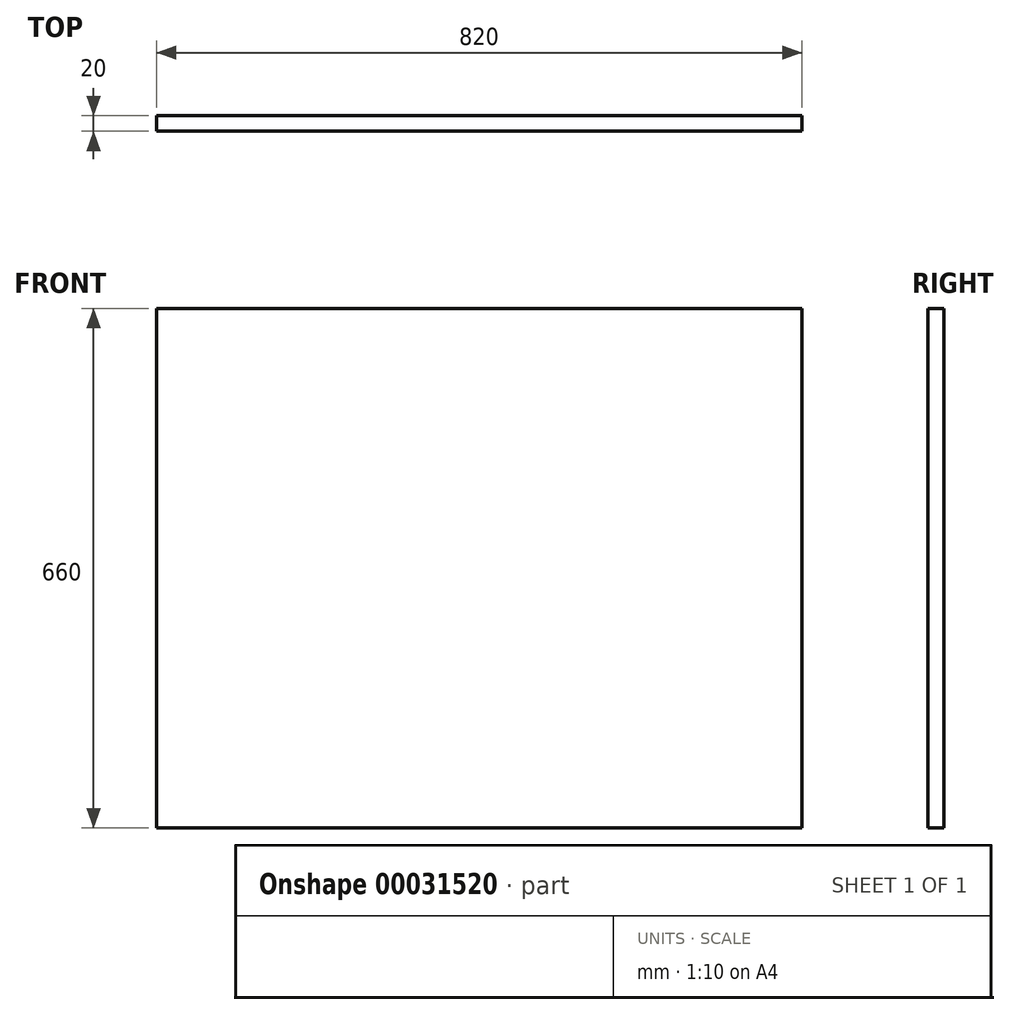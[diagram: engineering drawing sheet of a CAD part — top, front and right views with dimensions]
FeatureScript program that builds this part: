
annotation { "Feature Type Name" : "Feature", "Feature Type Description" : "" }
export const myFeature = defineFeature(function(context is Context, id is Id, definition is map)
    precondition{}
    {
        {
            var Q0;
            Q0=qCreatedBy(makeId("Front.planeOp"),FACE);
            var sketch = newSketch(context, id + "F0", { "sketchPlane" : qUnion([Q0])});
            skLineSegment(sketch, "E0.rect.bottom", {"start": v(410, 330) * mm, "end": v(-410, 330) * mm});
            skLineSegment(sketch, "E0.rect.top", {"start": v(410, -330) * mm, "end": v(-410, -330) * mm});
            skLineSegment(sketch, "E0.rect.left", {"start": v(410, 330) * mm, "end": v(410, -330) * mm});
            skLineSegment(sketch, "E0.rect.right", {"start": v(-410, 330) * mm, "end": v(-410, -330) * mm});
            skPoint(sketch, "E0.rect.middle", {"position": v(0, 0) * mm});
            skSolve(sketch);
        }
        {
            var Q0;
            Q0 = qSketchRegion(id + "F0", true);
            extrude(context, id + "F1", {"entities" : qUnion([Q0]), "oppositeDirection" : true, "depth" : 20 * mm});
        }
    });
